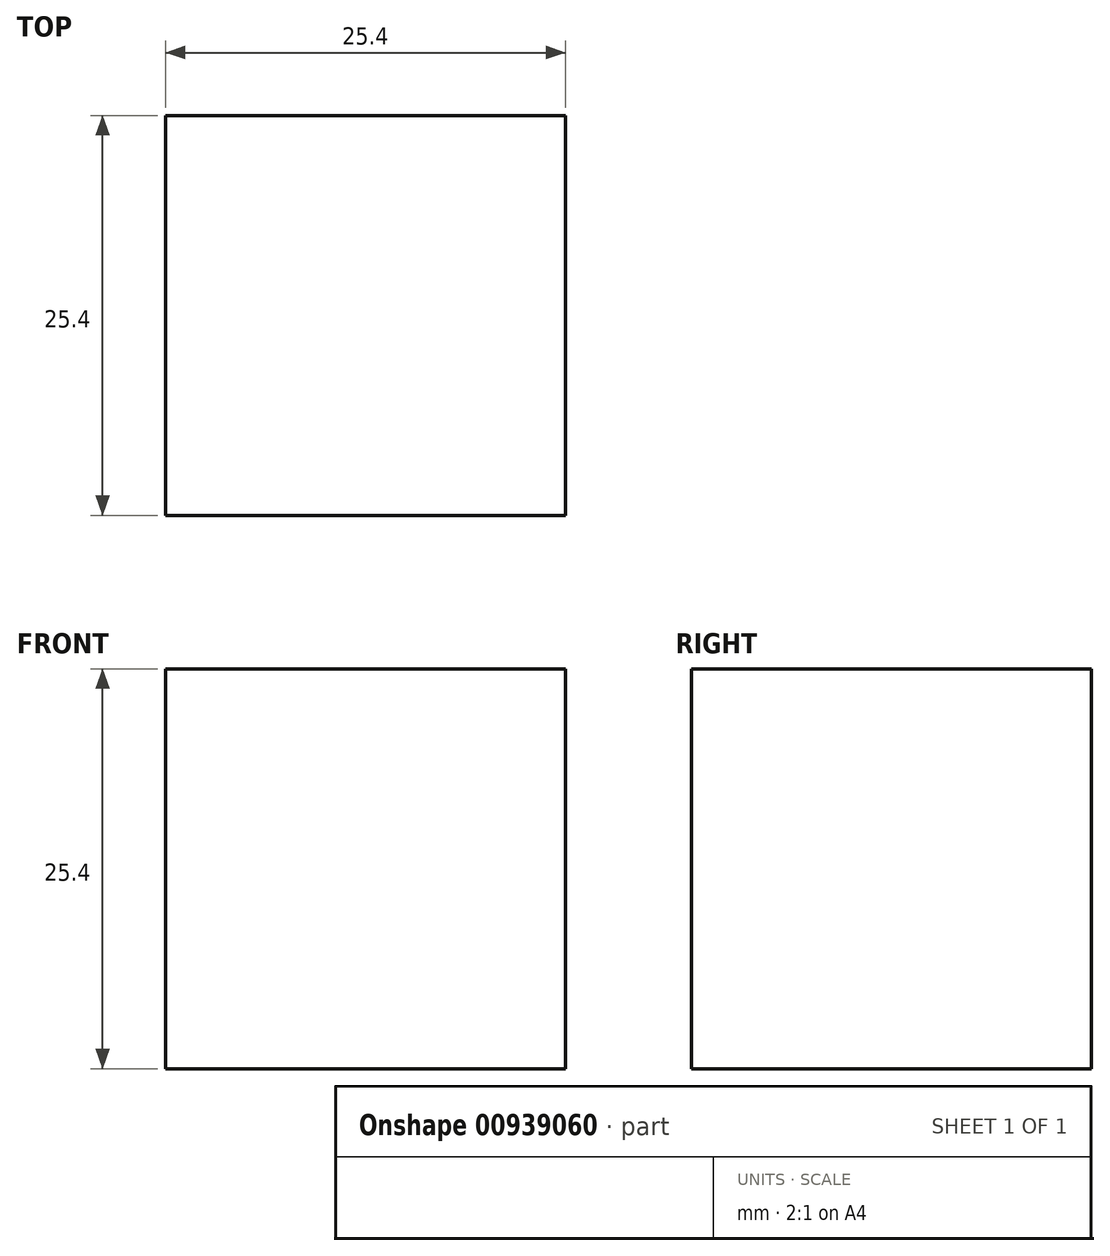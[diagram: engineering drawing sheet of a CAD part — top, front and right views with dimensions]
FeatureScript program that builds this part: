
annotation { "Feature Type Name" : "Feature", "Feature Type Description" : "" }
export const myFeature = defineFeature(function(context is Context, id is Id, definition is map)
    precondition{}
    {
        {
            var Q0;
            Q0=qCreatedBy(makeId("Top.planeOp"),FACE);
            var sketch = newSketch(context, id + "F0", { "sketchPlane" : qUnion([Q0])});
            skLineSegment(sketch, "E0", {"start": v(0, 0) * mm, "end": v(0, 25.4) * mm});
            skLineSegment(sketch, "E1", {"start": v(0, 25.4) * mm, "end": v(25.4, 25.4) * mm});
            skLineSegment(sketch, "E2", {"start": v(25.4, 25.4) * mm, "end": v(25.4, 0) * mm});
            skLineSegment(sketch, "E3", {"start": v(25.4, 0) * mm, "end": v(0, 0) * mm});
            skSolve(sketch);
        }
        {
            var Q0;
            Q0 = qSketchRegion(id + "F0", true);
            var Q1;
            Q1=makeQuery(id+"F0.imprint","IMPRINT",FACE,{"disambiguationData":[TD([[makeQuery(id+"F0.imprint","IMPRINT",EDGE,{"derivedFrom":sQuery(id+"F0.wireOp",EDGE,"E0")}),-1.0]])]});
            extrude(context, id + "F1", {"entities" : qUnion([Q0, Q1]), "depth" : 25.4 * mm, "offsetDistance" : 25.4 * mm});
        }
    });
